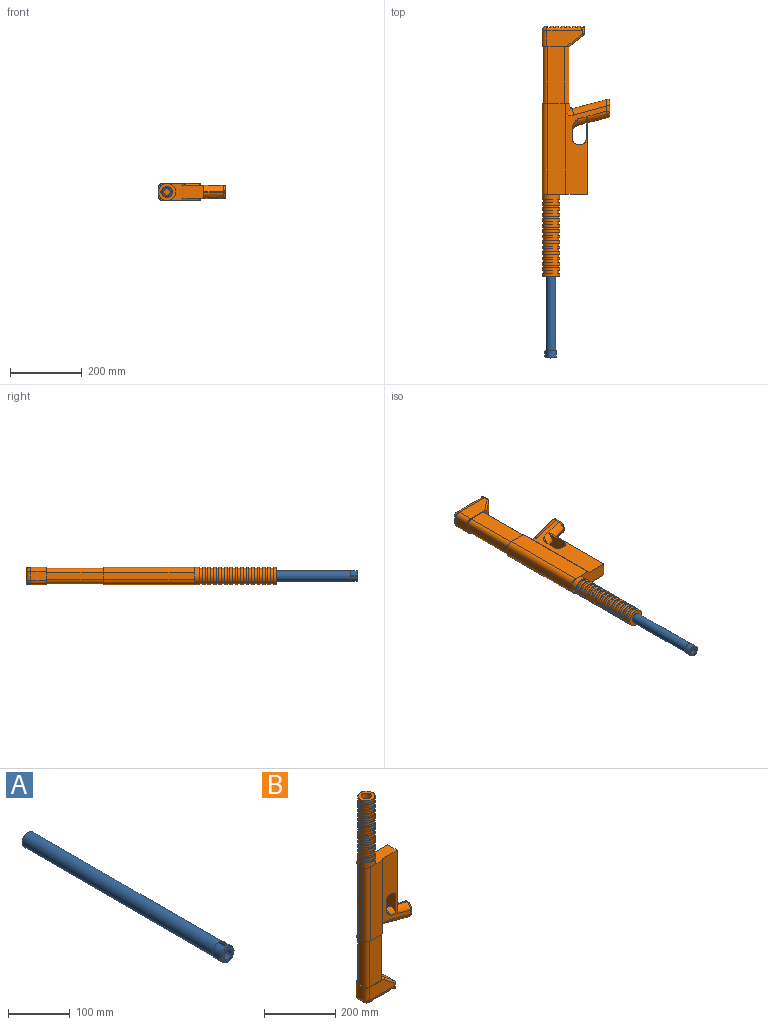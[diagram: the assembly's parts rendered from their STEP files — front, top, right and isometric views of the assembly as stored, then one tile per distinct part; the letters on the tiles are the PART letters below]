
ASSEMBLY  parts=2 mates=1
PART A: 19 faces, bbox 30x457.2x32.9 mm
  f0: plane 4.06x2.54mm, normal (0,0,1), area 10.3mm2, adj f7,f9,f18
  f1: cylinder r=13.97mm len=436.88mm, axis (0,1,0), area 38347.6mm2, adj f5,f9
  f2: cylinder r=8.89mm len=457.2mm, axis (0,1,0), area 25538.1mm2, adj f4,f5
  f3: cylinder r=13.97mm len=27.94mm, axis (0,1,0), area 223mm2, adj f4,f8
  f4: plane 27.94x27.94mm, normal (0,-1,0), area 364.8mm2, adj f2,f3
  f5: plane 27.94x27.94mm, normal (0,1,0), area 364.8mm2, adj f1,f2
  f6: plane 4.06x2.54mm, normal (0,0,1), area 10.3mm2, adj f7,f8,f17
  f7: cylinder r=14.99mm len=29.97mm, axis (0,1,0), area 1601.7mm2, adj f0,f6,f8,f9,f10,f16
  f8: plane 29.97x29.83mm, normal (0,-1,0), area 92mm2, adj f3,f6,f7
  f9: plane 29.97x29.83mm, normal (0,1,0), area 92mm2, adj f0,f1,f7
  f10: plane 12.7x3.05mm, normal (1,0,0), area 38.7mm2, adj f7,f11,f17,f18
  f11: plane 12.7x1.55mm, normal (0,0,1), area 19.7mm2, adj f10,f12,f17,f18
  f12: plane 12.7x0.89mm, normal (-0.98,0,-0.17), area 11.5mm2, adj f11,f13,f17,f18
  f13: plane 12.7x1.27mm, normal (0,0,1), area 16.1mm2, adj f12,f14,f17,f18
  f14: plane 12.7x0.89mm, normal (0.98,0,-0.17), area 11.5mm2, adj f13,f15,f17,f18
  f15: plane 12.7x1.55mm, normal (0,0,1), area 19.7mm2, adj f14,f16,f17,f18
  f16: plane 12.7x3.05mm, normal (-1,0,0), area 38.7mm2, adj f7,f15,f17,f18
  f17: plane 4.06x3.05mm, normal (0,-1,0), area 11.4mm2, adj f6,f10,f11,f12,f13,f14,f15,f16
  f18: plane 4.06x3.05mm, normal (0,1,0), area 11.4mm2, adj f0,f10,f11,f12,f13,f14,f15,f16
PART B: 175 faces, bbox 204.3x75x704.9 mm
  f0: plane 76.2x48.26mm, normal (0,0,-1), area 545.3mm2, adj f1,f5,f67,f68,f69,f77,f104,f105
  f1: plane 254x48.26mm, normal (0,-1,0), area 12258mm2, adj f0,f66,f67,f70,f104
  f2: plane 221.28x41.41mm, normal (1,0,0), area 3876.3mm2, adj f70,f73,f75,f76,f81,f83,f84,f91
  f3: plane 38.1x12.14mm, normal (0,0,-1), area 462.5mm2, adj f83,f84,f173,f174
  f4: plane 38.11x31mm, normal (1,0,0), area 997.3mm2, adj f83,f84,f101,f102,f103,f174
  f5: plane 254x48.26mm, normal (0,1,0), area 12258mm2, adj f0,f65,f69,f70,f105
  f6: cylinder r=13.97mm len=482.6mm, axis (0,0,1), area 37110mm2, adj f64,f71,f72,f73,f74,f152
  f7: cylinder r=24.13mm len=48.26mm, axis (0,0,1), area 2310.6mm2, adj f8,f65,f66,f70
  f8: plane 48.26x48.26mm, normal (0,0,1), area 364.8mm2, adj f7,f9
  f9: cylinder r=21.59mm len=43.18mm, axis (0,0,1), area 1033.7mm2, adj f8,f10
  f10: plane 48.26x48.26mm, normal (0,0,-1), area 364.8mm2, adj f9,f11
  f11: cylinder r=24.13mm len=48.26mm, axis (0,0,1), area 1155.3mm2, adj f10,f12
  f12: plane 48.26x48.26mm, normal (0,0,1), area 364.8mm2, adj f11,f13
  f13: cylinder r=21.59mm len=43.18mm, axis (0,0,1), area 1033.7mm2, adj f12,f14
  f14: plane 48.26x48.26mm, normal (0,0,-1), area 364.8mm2, adj f13,f15
  f15: cylinder r=24.13mm len=48.26mm, axis (0,0,1), area 1155.3mm2, adj f14,f16
  f16: plane 48.26x48.26mm, normal (0,0,1), area 364.8mm2, adj f15,f17
  f17: cylinder r=21.59mm len=43.18mm, axis (0,0,1), area 1033.7mm2, adj f16,f18
  f18: plane 48.26x48.26mm, normal (0,0,-1), area 364.8mm2, adj f17,f19
  f19: cylinder r=24.13mm len=48.26mm, axis (0,0,1), area 1155.3mm2, adj f18,f20
  f20: plane 48.26x48.26mm, normal (0,0,1), area 364.8mm2, adj f19,f21
  f21: cylinder r=21.59mm len=43.18mm, axis (0,0,1), area 1033.7mm2, adj f20,f22
  f22: plane 48.26x48.26mm, normal (0,0,-1), area 364.8mm2, adj f21,f23
  f23: cylinder r=24.13mm len=48.26mm, axis (0,0,1), area 1155.3mm2, adj f22,f24
  f24: plane 48.26x48.26mm, normal (0,0,1), area 364.8mm2, adj f23,f25
  f25: cylinder r=21.59mm len=43.18mm, axis (0,0,1), area 1033.7mm2, adj f24,f26
  f26: plane 48.26x48.26mm, normal (0,0,-1), area 364.8mm2, adj f25,f27
  f27: cylinder r=24.13mm len=48.26mm, axis (0,0,1), area 1155.3mm2, adj f26,f28
  f28: plane 48.26x48.26mm, normal (0,0,1), area 364.8mm2, adj f27,f29
  f29: cylinder r=21.59mm len=43.18mm, axis (0,0,1), area 1033.7mm2, adj f28,f30
  f30: plane 48.26x48.26mm, normal (0,0,-1), area 364.8mm2, adj f29,f31
  f31: cylinder r=24.13mm len=48.26mm, axis (0,0,1), area 1155.3mm2, adj f30,f32
  f32: plane 48.26x48.26mm, normal (0,0,1), area 364.8mm2, adj f31,f33
  f33: cylinder r=21.59mm len=43.18mm, axis (0,0,1), area 1033.7mm2, adj f32,f34
  f34: plane 48.26x48.26mm, normal (0,0,-1), area 364.8mm2, adj f33,f35
  f35: cylinder r=24.13mm len=48.26mm, axis (0,0,1), area 1155.3mm2, adj f34,f36
  f36: plane 48.26x48.26mm, normal (0,0,1), area 364.8mm2, adj f35,f37
  f37: cylinder r=21.59mm len=43.18mm, axis (0,0,1), area 1033.7mm2, adj f36,f38
  f38: plane 48.26x48.26mm, normal (0,0,-1), area 364.8mm2, adj f37,f39
  f39: cylinder r=24.13mm len=48.26mm, axis (0,0,1), area 1155.3mm2, adj f38,f40
  f40: plane 48.26x48.26mm, normal (0,0,1), area 364.8mm2, adj f39,f41
  f41: cylinder r=21.59mm len=43.18mm, axis (0,0,1), area 1033.7mm2, adj f40,f42
  f42: plane 48.26x48.26mm, normal (0,0,-1), area 364.8mm2, adj f41,f43
  f43: cylinder r=24.13mm len=48.26mm, axis (0,0,1), area 1155.3mm2, adj f42,f44
  f44: plane 48.26x48.26mm, normal (0,0,1), area 364.8mm2, adj f43,f45
  f45: cylinder r=21.59mm len=43.18mm, axis (0,0,1), area 1033.7mm2, adj f44,f46
  f46: plane 48.26x48.26mm, normal (0,0,-1), area 364.8mm2, adj f45,f47
  f47: cylinder r=24.13mm len=48.26mm, axis (0,0,1), area 1155.3mm2, adj f46,f48
  f48: plane 48.26x48.26mm, normal (0,0,1), area 364.8mm2, adj f47,f49
  f49: cylinder r=21.59mm len=43.18mm, axis (0,0,1), area 1033.7mm2, adj f48,f50
  f50: plane 48.26x48.26mm, normal (0,0,-1), area 364.8mm2, adj f49,f51
  f51: cylinder r=24.13mm len=48.26mm, axis (0,0,1), area 1155.3mm2, adj f50,f52
  f52: plane 48.26x48.26mm, normal (0,0,1), area 364.8mm2, adj f51,f53
  f53: cylinder r=21.59mm len=43.18mm, axis (0,0,1), area 1033.7mm2, adj f52,f54
  f54: plane 48.26x48.26mm, normal (0,0,-1), area 364.8mm2, adj f53,f55
  f55: cylinder r=24.13mm len=48.26mm, axis (0,0,1), area 1155.3mm2, adj f54,f56
  f56: plane 48.26x48.26mm, normal (0,0,1), area 364.8mm2, adj f55,f57
  f57: cylinder r=21.59mm len=43.18mm, axis (0,0,1), area 1033.7mm2, adj f56,f58
  f58: plane 48.26x48.26mm, normal (0,0,-1), area 364.8mm2, adj f57,f59
  f59: cylinder r=24.13mm len=48.26mm, axis (0,0,1), area 1155.3mm2, adj f58,f60
  f60: plane 48.26x48.26mm, normal (0,0,1), area 364.8mm2, adj f59,f61
  f61: cylinder r=21.59mm len=43.18mm, axis (0,0,1), area 1033.7mm2, adj f60,f62
  f62: plane 48.26x48.26mm, normal (0,0,-1), area 364.8mm2, adj f61,f63
  f63: cylinder r=24.13mm len=48.26mm, axis (0,0,1), area 1155.3mm2, adj f62,f64
  f64: plane 48.26x48.26mm, normal (0,0,1), area 1216.1mm2, adj f6,f63
  f65: plane 24.13x24.13mm, normal (0,0,1), area 75.1mm2, adj f5,f7,f68,f69
  f66: plane 24.13x24.13mm, normal (0,0,1), area 75.1mm2, adj f1,f7,f67,f68
  f67: cylinder r=15.24mm len=254mm, axis (0,0,1), area 6080.5mm2, adj f0,f1,f66,f68
  f68: plane 254x17.78mm, normal (-1,0,0), area 4516.1mm2, adj f0,f65,f66,f67,f69
  f69: cylinder r=15.24mm len=254mm, axis (0,0,1), area 6080.5mm2, adj f0,f5,f65,f68
  f70: plane 102.87x48.26mm, normal (0,0,1), area 3430.5mm2, adj f1,f2,f5,f7,f83,f84,f104,f105
  f71: plane 127x0.06mm, normal (1,0,0), area 7.3mm2, adj f6,f73,f74,f76
  f72: plane 127x0.06mm, normal (1,0,0), area 7.3mm2, adj f6,f73,f74,f75
  f73: plane 101.6x27.94mm, normal (0,0,-1), area 2567.6mm2, adj f2,f6,f71,f72,f75,f76
  f74: plane 88.9x27.94mm, normal (0,0,1), area 2212.7mm2, adj f6,f71,f72,f75,f76,f106
  f75: plane 139.7x101.6mm, normal (0,1,0), area 12937.8mm2, adj f2,f72,f73,f74,f106
  f76: plane 139.7x101.6mm, normal (0,-1,0), area 12937.8mm2, adj f2,f71,f73,f74,f106
  f77: plane 23.06x7.98mm, normal (1,0,0), area 134mm2, adj f0,f104,f105,f167,f168,f169
  f78: plane 93.69x25.1mm, normal (-0.26,0,-0.97), area 246.4mm2, adj f86,f88,f93,f171
  f79: plane 26.24x7.03mm, normal (0.26,0,0.97), area 69mm2, adj f80,f89,f90,f102
  f80: plane 67.52x41.41mm, normal (-1,0,0), area 1927.7mm2, adj f79,f83,f84,f89,f90,f173
  f81: plane 55.31x14.82mm, normal (0.26,0,0.97), area 145.4mm2, adj f2,f91,f92,f96
  f82: plane 35.75x23.59mm, normal (1,0,0), area 781.9mm2, adj f93,f94,f95,f96,f97,f98,f99,f100
  f83: plane 251.98x117.49mm, normal (0,-1,0), area 11356.4mm2, adj f2,f3,f4,f70,f80,f85,f86,f89
  f84: plane 251.97x117.48mm, normal (0,1,0), area 11356.3mm2, adj f2,f3,f4,f70,f80,f87,f88,f90
  f85: bspline ~18.55x17.78mm, area 215mm2, adj f83,f86,f104
  f86: bspline ~119.85x48.06mm, area 2605.5mm2, adj f78,f83,f85,f97,f104,f172
  f87: bspline ~18.55x17.78mm, area 215mm2, adj f84,f88,f105
  f88: bspline ~119.85x48.06mm, area 2605.5mm2, adj f78,f84,f87,f98,f105,f170
  f89: bspline ~50.96x29.6mm, area 676.1mm2, adj f79,f80,f83,f103
  f90: bspline ~50.96x29.6mm, area 676.1mm2, adj f79,f80,f84,f101
  f91: bspline ~76.72x36.5mm, area 1504.7mm2, adj f2,f81,f83,f99
  f92: bspline ~76.72x36.5mm, area 1504.7mm2, adj f2,f81,f84,f100
  f93: bspline ~22.86x9.59mm, area 151.5mm2, adj f78,f82,f97,f98
  f94: bspline ~35.02x7.62mm, area 251.6mm2, adj f82,f83,f97,f99
  f95: bspline ~35.02x7.62mm, area 251.6mm2, adj f82,f84,f98,f100
  f96: bspline ~22.86x7.36mm, area 70.1mm2, adj f81,f82,f99,f100
  f97: bspline ~19.08x18.21mm, area 240.3mm2, adj f82,f86,f93,f94
  f98: bspline ~19.08x18.29mm, area 239mm2, adj f82,f88,f93,f95
  f99: bspline ~20.22x20.17mm, area 182.8mm2, adj f82,f83,f91,f94,f96
  f100: bspline ~20.53x20.38mm, area 184.8mm2, adj f82,f84,f92,f95,f96
  f101: bspline ~39.68x35.83mm, area 522.3mm2, adj f4,f84,f90,f102
  f102: cylinder r=15.24mm len=14.72mm, axis (0,-1,0), area 50.7mm2, adj f4,f79,f101,f103
  f103: bspline ~39.68x35.83mm, area 522.3mm2, adj f4,f83,f89,f102
  f104: plane 260.43x27.62mm, normal (0.71,-0.71,0), area 2123mm2, adj f0,f1,f70,f77,f83,f85,f86,f169
  f105: plane 260.43x27.62mm, normal (0.71,0.71,0), area 2122.9mm2, adj f0,f5,f70,f77,f84,f87,f88,f167
  f106: cylinder r=12.7mm len=27.94mm, axis (0,-1,0), area 557.4mm2, adj f2,f74,f75,f76
  f107: plane 158.6x46.99mm, normal (0,1,0), area 7452.5mm2, adj f0,f151,f159,f162
  f108: plane 158.6x46.99mm, normal (0,-1,0), area 7452.5mm2, adj f0,f151,f160,f161
  f109: plane 158.6x17.78mm, normal (-1,0,0), area 2819.9mm2, adj f0,f151,f159,f160
  f110: plane 158.6x20.32mm, normal (1,0,0), area 3222.7mm2, adj f0,f151,f161,f162
  f111: sphere r=5.08mm, area 17.4mm2, adj f112,f148,f149
  f112: cylinder r=5.08mm len=16.61mm, axis (0,0,-1), area 152.8mm2, adj f111,f116,f147,f150,f155,f164
  f113: cylinder r=5.08mm len=38.1mm, axis (0,-1,0), area 173.6mm2, adj f118,f150,f164,f166
  f114: cylinder r=5.08mm len=16.61mm, axis (0,0,1), area 152.8mm2, adj f115,f117,f147,f150,f158,f166
  f115: sphere r=5.08mm, area 17.4mm2, adj f114,f148,f149
  f116: plane 99.94x44.6mm, normal (0,1,0), area 3663.7mm2, adj f112,f151,f153,f155,f163
  f117: plane 99.94x44.6mm, normal (0,-1,0), area 3663.7mm2, adj f114,f151,f156,f158,f165
  f118: plane 39.61x38.1mm, normal (0.62,0,0.78), area 1931.7mm2, adj f113,f151,f163,f165
  f119: plane 44.6x22.86mm, normal (-1,0,0), area 1019.6mm2, adj f120,f151,f153,f156
  f120: cylinder r=12.7mm len=22.86mm, axis (0,1,0), area 456mm2, adj f119,f121,f154,f157
  f121: plane 22.86x2.54mm, normal (0,0,-1), area 58.1mm2, adj f120,f122,f155,f158
  f122: plane 43.18x5.08mm, normal (1,0,0), area 188.3mm2, adj f121,f123,f155,f158
  f123: plane 43.18x7.62mm, normal (0,0,-1), area 329mm2, adj f122,f124,f155,f158
  f124: plane 43.18x5.08mm, normal (-1,0,0), area 188.3mm2, adj f123,f125,f155,f158
  f125: plane 22.86x7.62mm, normal (0,0,-1), area 174.2mm2, adj f124,f126,f155,f158
  f126: plane 43.18x5.08mm, normal (1,0,0), area 188.3mm2, adj f125,f127,f155,f158
  f127: plane 43.18x7.62mm, normal (0,0,-1), area 329mm2, adj f126,f128,f155,f158
  f128: plane 43.18x5.08mm, normal (-1,0,0), area 188.3mm2, adj f127,f129,f155,f158
  f129: plane 22.86x7.62mm, normal (0,0,-1), area 174.2mm2, adj f128,f130,f155,f158
  f130: plane 43.18x5.08mm, normal (1,0,0), area 188.3mm2, adj f129,f131,f155,f158
  f131: plane 43.18x7.62mm, normal (0,0,-1), area 329mm2, adj f130,f132,f155,f158
  f132: plane 43.18x5.08mm, normal (-1,0,0), area 188.3mm2, adj f131,f133,f155,f158
  f133: plane 22.86x7.62mm, normal (0,0,-1), area 174.2mm2, adj f132,f134,f155,f158
  f134: plane 43.18x5.08mm, normal (1,0,0), area 188.3mm2, adj f133,f135,f155,f158
  f135: plane 43.18x7.62mm, normal (0,0,-1), area 329mm2, adj f134,f136,f155,f158
  f136: plane 43.18x5.08mm, normal (-1,0,0), area 188.3mm2, adj f135,f137,f155,f158
  f137: plane 22.86x7.62mm, normal (0,0,-1), area 174.2mm2, adj f136,f138,f155,f158
  f138: plane 43.18x5.08mm, normal (1,0,0), area 188.3mm2, adj f137,f139,f155,f158
  f139: plane 43.18x7.62mm, normal (0,0,-1), area 329mm2, adj f138,f140,f155,f158
  f140: plane 43.18x5.08mm, normal (-1,0,0), area 188.3mm2, adj f139,f141,f155,f158
  f141: plane 22.86x7.62mm, normal (0,0,-1), area 174.2mm2, adj f140,f142,f155,f158
  f142: plane 43.18x5.08mm, normal (1,0,0), area 188.3mm2, adj f141,f143,f155,f158
  f143: plane 43.18x7.62mm, normal (0,0,-1), area 329mm2, adj f142,f144,f155,f158
  f144: plane 43.18x5.08mm, normal (-1,0,0), area 188.3mm2, adj f143,f145,f155,f158
  f145: plane 22.86x7.62mm, normal (0,0,-1), area 174.2mm2, adj f144,f146,f155,f158
  f146: plane 43.18x5.08mm, normal (1,0,0), area 188.3mm2, adj f145,f147,f155,f158
  f147: plane 48.26x7.62mm, normal (0,0,-1), area 353mm2, adj f112,f114,f146,f148,f155,f158
  f148: plane 51.77x8.87mm, normal (-1,0,0), area 219.1mm2, adj f111,f115,f147,f149
  f149: cylinder r=5.08mm len=38.1mm, axis (0,1,0), area 239.6mm2, adj f111,f115,f148,f150
  f150: plane 38.1x16.61mm, normal (1,0,0), area 632.7mm2, adj f112,f113,f114,f149
  f151: plane 78.87x50.93mm, normal (0,0,1), area 719.4mm2, adj f107,f108,f109,f110,f116,f117,f118,f119
  f152: plane 27.94x27.94mm, normal (0,0,1), area 613.1mm2, adj f6
  f153: cylinder r=12.7mm len=44.6mm, axis (0,0,1), area 889.8mm2, adj f116,f119,f151,f154
  f154: sphere r=12.7mm, area 162.5mm2, adj f120,f153,f155
  f155: cylinder r=12.7mm len=99.94mm, axis (-1,0,0), area 1367.1mm2, adj f112,f116,f121,f122,f123,f124,f125,f126
  f156: cylinder r=12.7mm len=44.6mm, axis (0,0,-1), area 889.8mm2, adj f117,f119,f151,f157
  f157: sphere r=12.7mm, area 345.4mm2, adj f120,f156,f158
  f158: cylinder r=12.7mm len=99.94mm, axis (1,0,0), area 1367.1mm2, adj f114,f117,f121,f122,f123,f124,f125,f126
  f159: cylinder r=12.7mm len=158.6mm, axis (0,0,1), area 3163.9mm2, adj f0,f107,f109,f151
  f160: cylinder r=12.7mm len=158.6mm, axis (0,0,-1), area 3163.9mm2, adj f0,f108,f109,f151
  f161: plane 158.6x11.43mm, normal (0.71,-0.71,0), area 2563.6mm2, adj f0,f108,f110,f151
  f162: plane 158.6x11.43mm, normal (0.71,0.71,0), area 2563.6mm2, adj f0,f107,f110,f151
  f163: cylinder r=5.08mm len=47.75mm, axis (0.78,0,-0.62), area 429.9mm2, adj f116,f118,f151,f164
  f164: sphere r=5.08mm, area 17mm2, adj f112,f113,f163
  f165: cylinder r=5.08mm len=47.75mm, axis (-0.78,0,0.62), area 429.9mm2, adj f117,f118,f151,f166
  f166: sphere r=5.08mm, area 23.1mm2, adj f113,f114,f165
  f167: bspline ~12.35x12.19mm, area 105.7mm2, adj f77,f105,f168,f170
  f168: cylinder r=10.16mm len=9.9mm, axis (0,-1,0), area 34.6mm2, adj f77,f167,f169,f171
  f169: bspline ~12.4x12.18mm, area 105.8mm2, adj f77,f104,f168,f172
  f170: bspline ~3.57x0.65mm, area 1.2mm2, adj f88,f105,f167,f171
  f171: cylinder r=1.27mm len=2.54mm, axis (0,-1,0), area 1.6mm2, adj f78,f168,f170,f172
  f172: bspline ~3.57x0.65mm, area 1.2mm2, adj f86,f104,f169,f171
  f173: cylinder r=12.7mm len=38.1mm, axis (0,-1,0), area 760.1mm2, adj f3,f80,f83,f84
  f174: cylinder r=12.7mm len=38.1mm, axis (0,-1,0), area 760.1mm2, adj f3,f4,f83,f84
PLACE A rot(axis=(0,-1,0),90deg) t=(-182.5,-50.8,0)mm
PLACE B rot(axis=(1,0,0),90deg) t=(-182.5,-228.6,0)mm
MATE fastened A.f2 <-> B.f6  axis (0,1,0) through (-182.5,-50.8,0)mm
